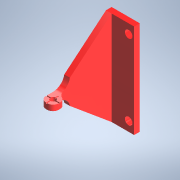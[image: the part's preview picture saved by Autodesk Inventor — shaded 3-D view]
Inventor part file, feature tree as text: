
AUTODESK INVENTOR PART (.ipt)
format: ipt  version: 2022 (Build 260153000, 153)  size: 202,752 bytes
history: native  units: mm
features: extrude x6, sketch x6, other x4, fillet x3, reference x2, projected_geometry x1
ambient origin geometry x8: Origin, YZ Plane, XZ Plane, XY Plane, X Axis, Y Axis, Z Axis, Center Point
bodies: Body1 (feature_tree)
feature tree (22):
  other  "Твердое тело1"
  extrude  "Выдавливание1"  Depth=15.0mm
  extrude  "Выдавливание2"  Depth=50.0mm
  extrude  "Выдавливание3"  Depth=40.0mm
  fillet  "Сопряжение1"  Radius=5.0mm
  fillet  "Сопряжение2"  Radius=3.0mm
  extrude  "Выдавливание4"  Depth=35.0mm
  extrude  "Выдавливание5"  Depth=30.0mm
  extrude  "Выдавливание6"  Depth=1.5mm
  fillet  "Сопряжение3"  Radius=1.5mm
  sketch  "Эскиз1"
  reference  "Ссылка1"
  reference  "Ссылка2"
  sketch  "Эскиз2"
  sketch  "Эскиз3"
  sketch  "Эскиз4"
  projected_geometry  "Спроецированная петля1"
  sketch  "Эскиз5"
  sketch  "Эскиз6"
  other  "<path> - Robot.iam"
  other  "000.000 - Robot.iam"
  other  "rpi3-bottom:1"
note: 1 file-system path scrubbed to <path> (originals preserved in map.json)
